# Revit family: _02HL_RU_Floor drain_HL510PrblueG
name_source: partatom
category: Instalační zařizovací předměty
units: mm (PartAtom-declared; Revit-internal decimal feet)

## family parameters
Bod výpočtu místnosti = Ano
Kóta kulaté spojky = Použít průměr
Nadpis OmniClass = Deck Waste Water Drains
Ořezat dutým tvarem při načtení = Ne
Sdílené = Ano
Typ dílu = Normální
Vždy vertikální = Ano
Založené na pracovní rovině = Ne
Číslo OmniClass = 23.70.50.21.24.14

## types (1)
- HL510PrblueG
    EAN = 9003076052172
    Indexovaná poznámka = HL510PrblueG
    Komentáře k typům = Трап для внутренних помещений DN40/50 горизонтальный с запахозапирающим устройством Primus blue, 150х150мм/137х137мм чугун
    Model = HL510PrblueG
    Popis = Трап для внутренних помещений
    Přípoj CW = Ne
    Přípoj HW = Ne
    Přípoj odpadních dílů = Ano
    Přípoj ventilace = Ne
    URL = https://www.hutterer-lechner.com
    Výchozí výška = 0 mm  [stored 0 ft]
    Výrobce = HL Hutterer & Lechner GmbH
    ВЕС = 2,43 [kg]
    ВЫСОТА МОНТАЖА = 123 mm
    МАКСИМАЛЬНАЯ НАГРУЗКА КЛАССА = L - 1,5 t
    МАТЕРИАЛ = PP, ABS, Guss
    НАСАДКА = 34-78 mm / 150 x 150 mm / Guss
    НОМИНАЛЬНЫЙ ДИАМЕТР = 50 mm
    Нормы = EN 1253-8
    ПРОИЗВОДИТЕЛЬНОСТЬ = 0,5 l/s
    РАЗМЕР = DN40/50
    РЕШЁТКА = 137 x 137 mm / Guss

note: [stored X ft] marks values corroborated as IEEE doubles in the binary element streams (Revit-internal decimal feet)

## geometry (parser evidence)
native form markers: Sweep x31
no freeform markers — native parametric forms only
